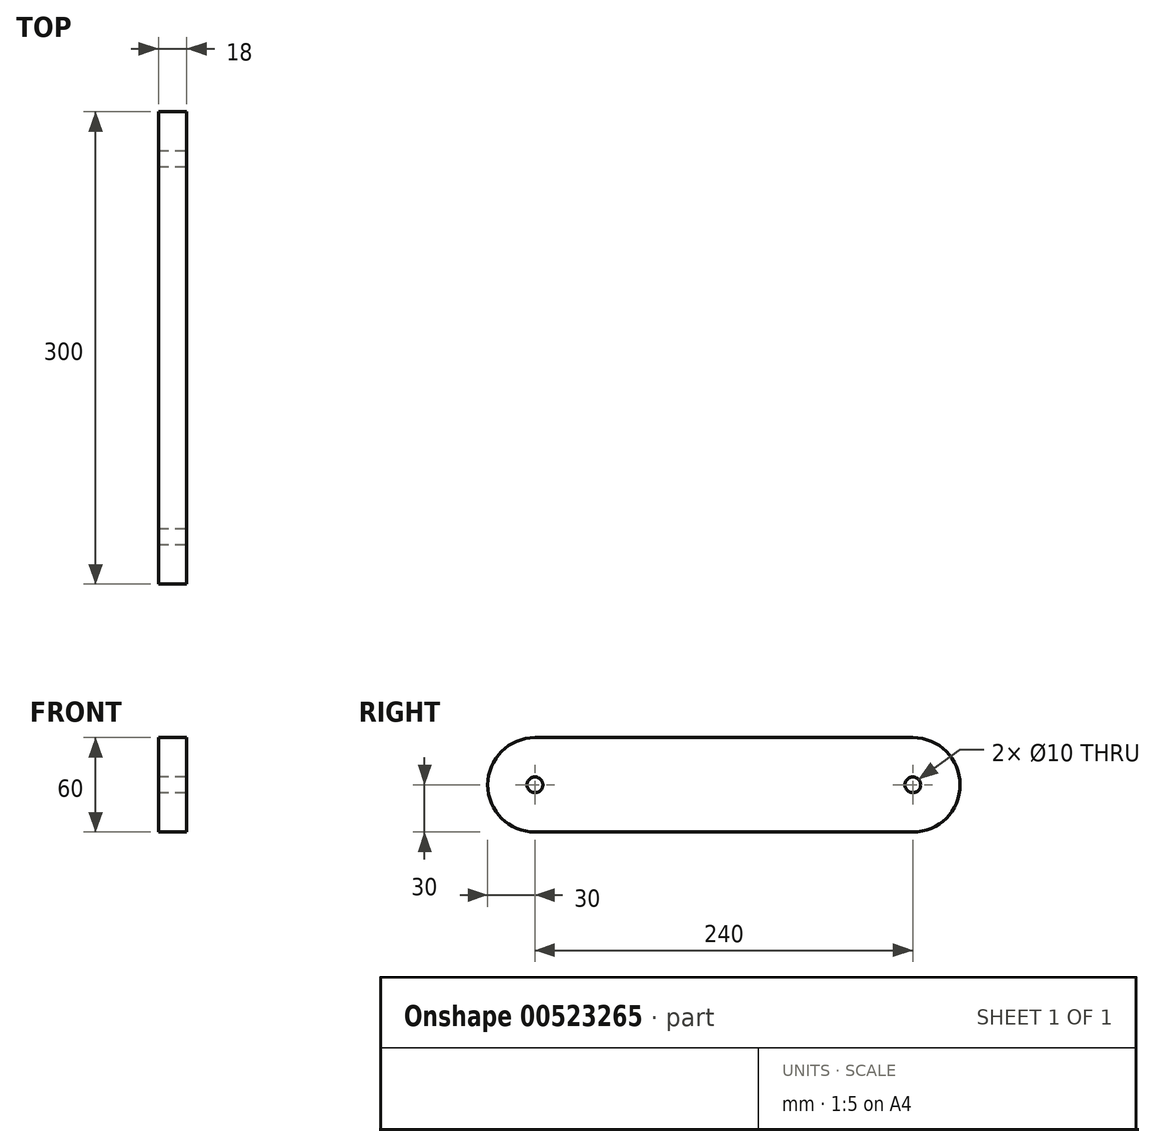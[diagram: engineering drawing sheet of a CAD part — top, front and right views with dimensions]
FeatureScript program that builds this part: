
annotation { "Feature Type Name" : "Feature", "Feature Type Description" : "" }
export const myFeature = defineFeature(function(context is Context, id is Id, definition is map)
    precondition{}
    {
        {
            var Q0;
            Q0=qCreatedBy(makeId("Right.planeOp"),FACE);
            var sketch = newSketch(context, id + "F0", { "sketchPlane" : qUnion([Q0])});
            skArc(sketch, "E0", {"start": v(0, 30) * mm, "mid": v(-30, 0) * mm, "end": v(0, -30) * mm});
            skLineSegment(sketch, "E1", {"start": v(0, 30) * mm, "end": v(240, 30) * mm});
            skLineSegment(sketch, "E2", {"start": v(0, -30) * mm, "end": v(240, -30) * mm});
            skArc(sketch, "E3", {"start": v(240, 30) * mm, "mid": v(270, 0) * mm, "end": v(240, -30) * mm});
            skCircle(sketch, "E4", {"center": v(0, 0) * mm, "radius": 5 * mm});
            skCircle(sketch, "E5", {"center": v(240, 0) * mm, "radius": 5 * mm});
            skSolve(sketch);
        }
        {
            var Q0;
            Q0=makeQuery(id+"F0.imprint","IMPRINT",FACE,{"disambiguationData":[TD([[makeQuery(id+"F0.imprint","IMPRINT",EDGE,{"derivedFrom":sQuery(id+"F0.wireOp",EDGE,"E0")}),1.0]])]});
            extrude(context, id + "F1", {"entities" : qUnion([Q0]), "depth" : 18 * mm, "offsetDistance" : 25 * mm});
        }
    });
